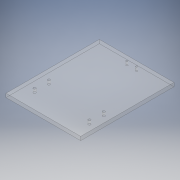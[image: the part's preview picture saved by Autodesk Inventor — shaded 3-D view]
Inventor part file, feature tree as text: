
AUTODESK INVENTOR PART (.ipt)
format: ipt  version: 2018 (Build 220112000, 112)  size: 127,488 bytes
history: native  units: in
note: dims shown in document units (in); Inventor stores cm internally (conversion verified against a paired STEP export)
features: sketch x3, hole x2, sheet_metal_op x1, other x1
ambient origin geometry x8: Origin, YZ Plane, XZ Plane, XY Plane, X Axis, Y Axis, Z Axis, Center Point
bodies: Solid1 (feature_tree)
feature tree (7):
  sheet_metal_op  "Face1"
  hole  "Hole1"  [1 undecoded]
  hole  "Hole2"  [1 undecoded]
  sketch  "Sketch1"  dims[d0=4.0in d1=5.0in]
  other  "Plate1"
  sketch  "Sketch2"  dims[d4=0.2in d5=0.77in]
  sketch  "Sketch3"  dims[d6=0.53in d7=0.129in d8=0.75in d9=0.279in d10=0.188in d11=0.5635in d12=0.2in d13=0.8108in d14=1.0in d15=1.0in d16=0.52in d17=0.09in d18=0.5in d19=0.375in d20=0.25in d21=0.5635in d22=0.2in d23=0.8108in]
note: 2 required parameter values undecoded (feature->parameter linkage not recoverable at this tier; creation-order binding heuristic only, values carry confidence <= 0.55)
